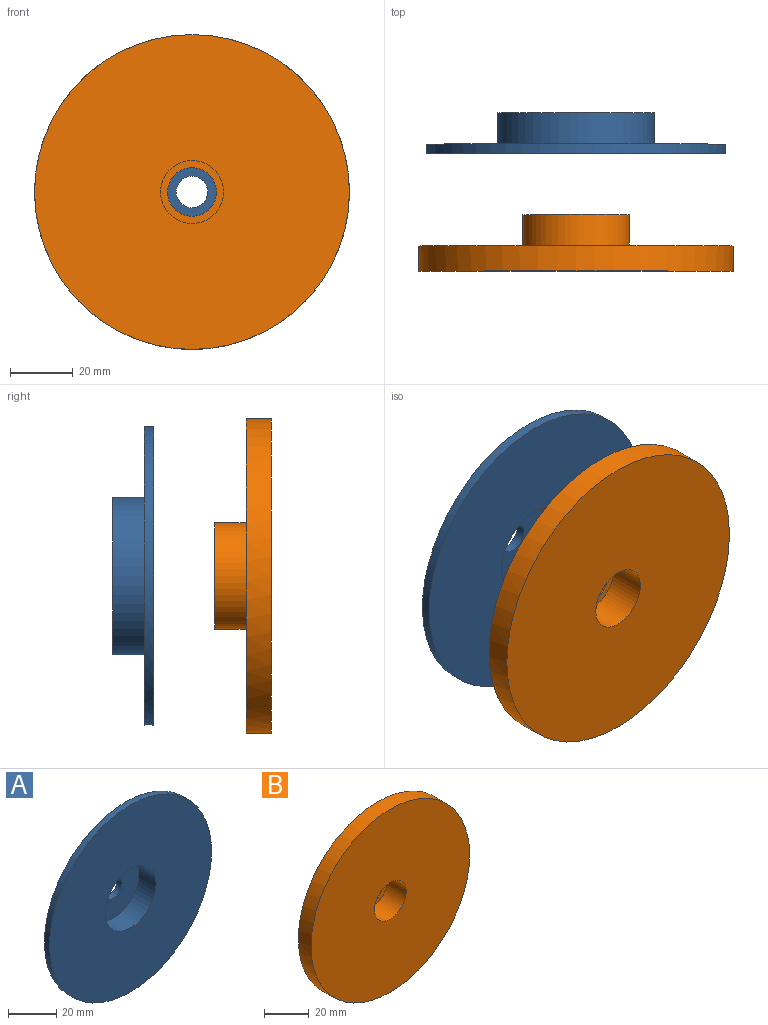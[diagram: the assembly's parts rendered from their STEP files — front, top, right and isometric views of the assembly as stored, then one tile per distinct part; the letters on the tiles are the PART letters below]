
ASSEMBLY  parts=2 mates=1
PART A: 8 faces, bbox 95x13x95 mm
  f0: cylinder r=47.5mm len=95mm, axis (0,1,0), area 895.4mm2, adj f1,f4
  f1: plane 95x95mm, normal (0,-1,0), area 6381.4mm2, adj f0,f2
  f2: cylinder r=15mm len=30mm, axis (0,-1,0), area 942.5mm2, adj f1,f3
  f3: plane 30x30mm, normal (0,-1,0), area 628.3mm2, adj f2,f7
  f4: plane 95x95mm, normal (0,1,0), area 5124.7mm2, adj f0,f5
  f5: cylinder r=25mm len=50mm, axis (0,1,0), area 1570.8mm2, adj f4,f6
  f6: plane 50x50mm, normal (0,1,0), area 1885mm2, adj f5,f7
  f7: cylinder r=5mm len=10mm, axis (0,1,0), area 94.2mm2, adj f3,f6
PART B: 8 faces, bbox 100x18x100 mm
  f0: cylinder r=50mm len=100mm, axis (0,1,0), area 2513.3mm2, adj f1,f4
  f1: plane 100x100mm, normal (0,1,0), area 6946.1mm2, adj f0,f2
  f2: cylinder r=17mm len=34mm, axis (0,1,0), area 1068.1mm2, adj f1,f3
  f3: plane 34x34mm, normal (0,1,0), area 719.2mm2, adj f2,f7
  f4: plane 100x100mm, normal (0,-1,0), area 7539.8mm2, adj f0,f5
  f5: cylinder r=10mm len=20mm, axis (0,-1,0), area 754mm2, adj f4,f6
  f6: plane 20x20mm, normal (0,-1,0), area 125.5mm2, adj f5,f7
  f7: cylinder r=7.75mm len=15.5mm, axis (0,1,0), area 292.2mm2, adj f3,f6
PLACE A t=(-8.65,-22.78,-61.95)mm
PLACE B t=(-8.65,-55.16,-61.95)mm
MATE cylindrical A.f2 <-> B.f2  axis (0,1,0) through (-8.65,-22.78,-61.95)mm
